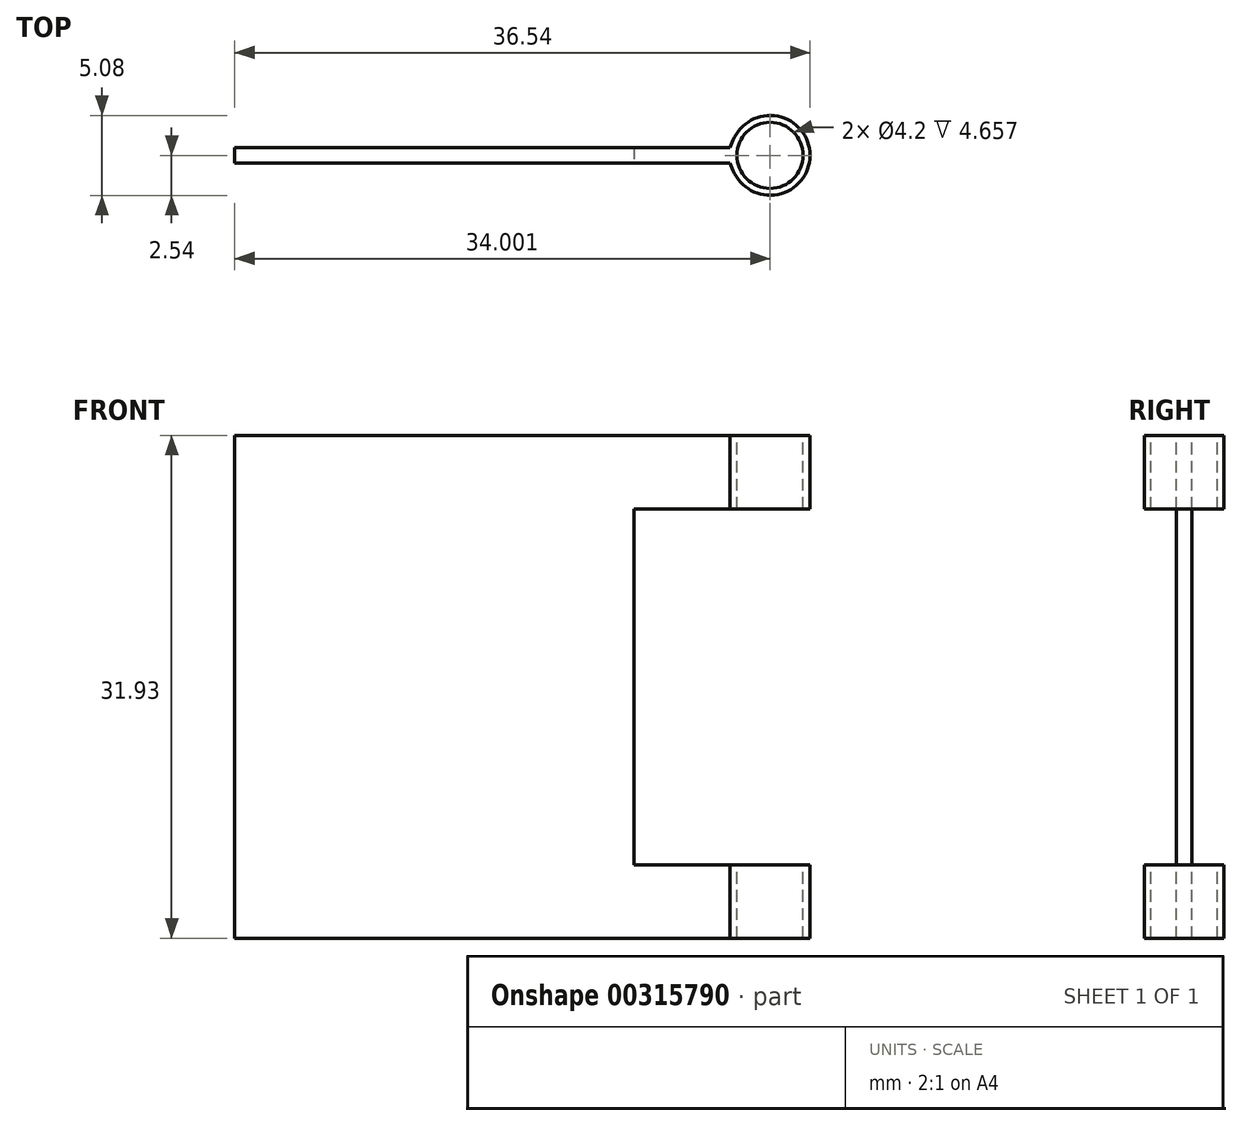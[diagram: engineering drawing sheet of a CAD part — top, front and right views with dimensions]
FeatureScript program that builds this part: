
annotation { "Feature Type Name" : "Feature", "Feature Type Description" : "" }
export const myFeature = defineFeature(function(context is Context, id is Id, definition is map)
    precondition{}
    {
        {
            var Q0;
            Q0=qCreatedBy(makeId("Front.planeOp"),FACE);
            var sketch = newSketch(context, id + "F0", { "sketchPlane" : qUnion([Q0])});
            skLineSegment(sketch, "E0.bottom", {"start": v(0, 0) * mm, "end": v(31.47, 0) * mm});
            skLineSegment(sketch, "E0.top", {"start": v(0, 31.93) * mm, "end": v(31.47, 31.93) * mm});
            skLineSegment(sketch, "E0.left", {"start": v(0, 0) * mm, "end": v(0, 31.93) * mm});
            skLineSegment(sketch, "E0.right", {"start": v(31.47, 0) * mm, "end": v(31.47, 31.93) * mm});
            skSolve(sketch);
        }
        {
            var Q0;
            Q0=makeQuery(id+"F0.imprint","IMPRINT",FACE,{"disambiguationData":[TD([[makeQuery(id+"F0.imprint","IMPRINT",EDGE,{"derivedFrom":sQuery(id+"F0.wireOp",EDGE,"E0.bottom")}),1.0]])]});
            extrude(context, id + "F1", {"entities" : qUnion([Q0]), "depth" : 1 * mm});
        }
        {
            var Q0;
            Q0=makeQuery(id+"F1.opExtrude","SWEPT_FACE",FACE,{"disambiguationData":[OSD([sQuery(id+"F0.wireOp",EDGE,"E0.top")])]});
            var sketch = newSketch(context, id + "F2", { "sketchPlane" : qUnion([Q0])});
            skArc(sketch, "E1", {"start": v(31.66, -1.46) * mm, "mid": v(36.54, -0.5) * mm, "end": v(31.66, 0.46) * mm});
            skPoint(sketch, "E1.centerSnap0", {"position": v(31.47, -0.5) * mm});
            skCircle(sketch, "E2", {"center": v(34, -0.5) * mm, "radius": 2.1 * mm});
            skLineSegment(sketch, "E3", {"start": v(31.47, -1) * mm, "end": v(31.66, -1.46) * mm});
            skLineSegment(sketch, "E4", {"start": v(31.47, 0) * mm, "end": v(31.66, 0.46) * mm});
            skSolve(sketch);
        }
        {
            var Q0;
            Q0=makeQuery(id+"F2.imprint","IMPRINT",FACE,{"disambiguationData":[TD([[makeQuery(id+"F2.imprint","IMPRINT",EDGE,{"derivedFrom":sQuery(id+"F2.wireOp",EDGE,"E1")}),1.0]])]});
            var Q1;
            Q1=makeQuery(id+"F1.opExtrude","SWEPT_FACE",FACE,{"disambiguationData":[OSD([sQuery(id+"F0.wireOp",EDGE,"E0.bottom")])]});
            extrude(context, id + "F3", {"entities" : qUnion([Q0]), "operationType" : NewBodyOperationType.ADD, "endBound" : BoundingType.UP_TO_SURFACE, "oppositeDirection" : true, "endBoundEntityFace" : qUnion([Q1]), "depth" : 25.4 * mm});
        }
        {
            var Q0;
            Q0=makeQuery(id+"F1.opExtrude","CAP_FACE",FACE,{"disambiguationData":[OSD([sQuery(id+"F0.wireOp",EDGE,"E0.bottom"),sQuery(id+"F0.wireOp",EDGE,"E0.top"),sQuery(id+"F0.wireOp",EDGE,"E0.left"),sQuery(id+"F0.wireOp",EDGE,"E0.right")])],"isStart":false});
            var sketch = newSketch(context, id + "F4", { "sketchPlane" : qUnion([Q0])});
            skLineSegment(sketch, "E5.bottom", {"start": v(37.56, 27.27) * mm, "end": v(25.37, 27.27) * mm});
            skLineSegment(sketch, "E5.top", {"start": v(37.56, 4.66) * mm, "end": v(25.37, 4.66) * mm});
            skLineSegment(sketch, "E5.left", {"start": v(37.56, 27.27) * mm, "end": v(37.56, 4.66) * mm});
            skLineSegment(sketch, "E5.right", {"start": v(25.37, 27.27) * mm, "end": v(25.37, 4.66) * mm});
            skPoint(sketch, "E5.middle", {"position": v(31.47, 15.96) * mm});
            skSolve(sketch);
        }
        {
            var Q0;
            Q0 = qSketchRegion(id + "F4", true);
            extrude(context, id + "F5", {"entities" : qUnion([Q0]), "operationType" : NewBodyOperationType.REMOVE, "endBound" : BoundingType.SYMMETRIC, "oppositeDirection" : true, "depth" : 7.62 * mm});
        }
    });
